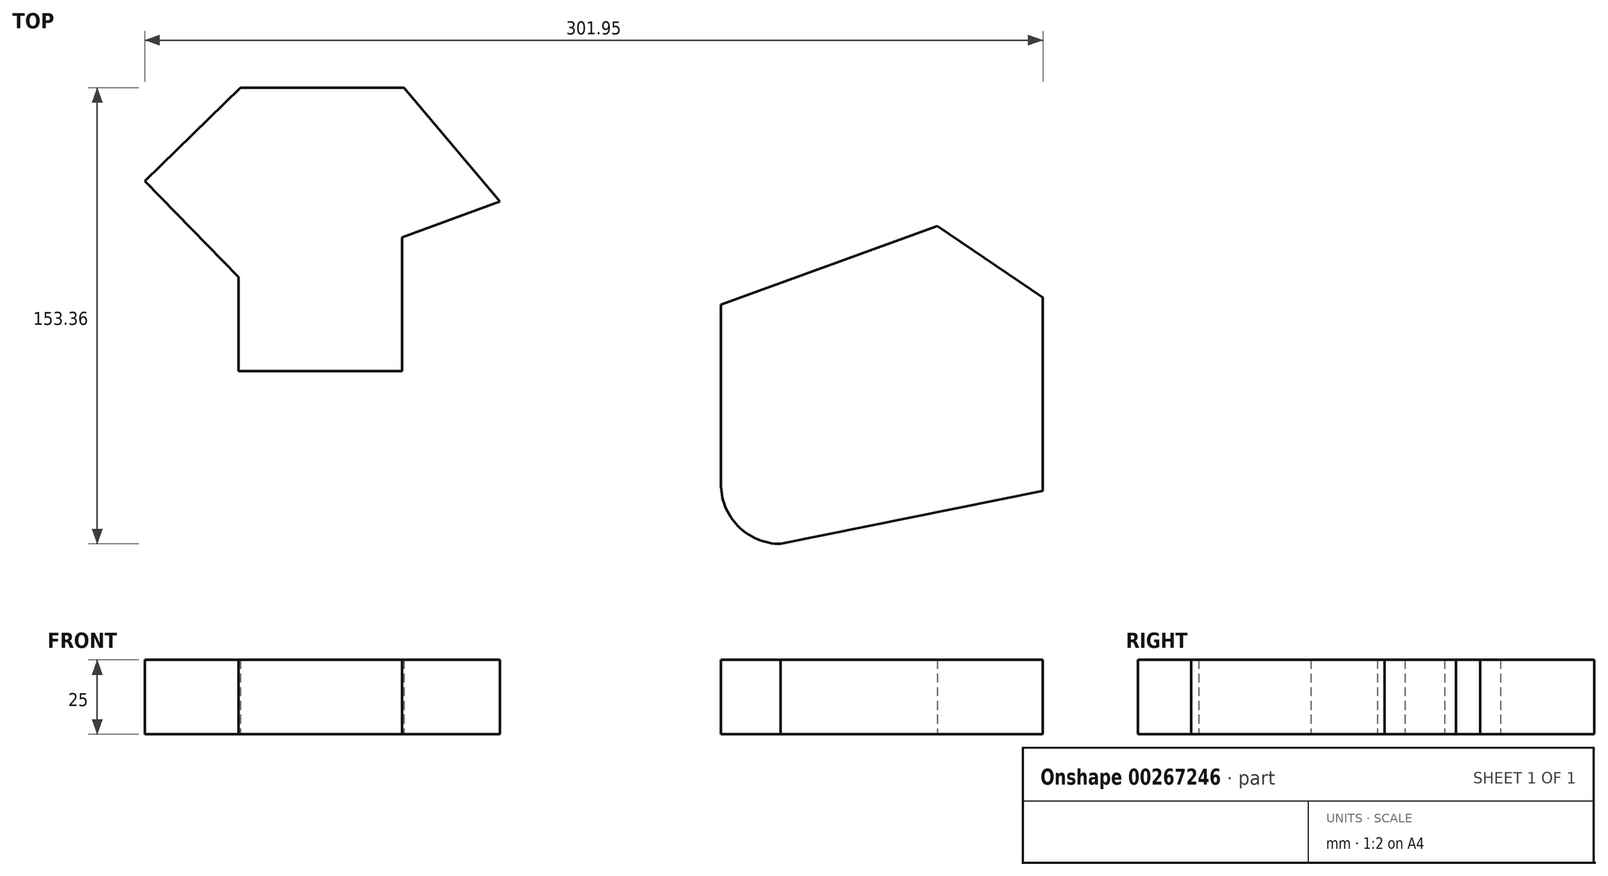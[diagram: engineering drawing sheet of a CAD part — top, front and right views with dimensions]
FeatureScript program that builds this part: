
annotation { "Feature Type Name" : "Feature", "Feature Type Description" : "" }
export const myFeature = defineFeature(function(context is Context, id is Id, definition is map)
    precondition{}
    {
        {
            var Q0;
            Q0=qCreatedBy(makeId("Top.planeOp"),FACE);
            var sketch = newSketch(context, id + "F0", { "sketchPlane" : qUnion([Q0])});
            skLineSegment(sketch, "E0", {"start": v(-58.1, 40.28) * mm, "end": v(-3.1, 40.28) * mm});
            skLineSegment(sketch, "E1", {"start": v(-3.1, 40.28) * mm, "end": v(-3.1, 85.28) * mm});
            skLineSegment(sketch, "E2", {"start": v(-3.1, 85.28) * mm, "end": v(29.78, 97.25) * mm});
            skLineSegment(sketch, "E3", {"start": v(29.78, 97.25) * mm, "end": v(-2.36, 135.55) * mm});
            skLineSegment(sketch, "E4", {"start": v(-2.36, 135.55) * mm, "end": v(-57.36, 135.55) * mm});
            skPoint(sketch, "E5.start.orphan", {"position": v(31.76, 97.25) * mm});
            skLineSegment(sketch, "E6", {"start": v(-57.36, 135.55) * mm, "end": v(-89.55, 104.1) * mm});
            skLineSegment(sketch, "E7", {"start": v(-89.55, 104.1) * mm, "end": v(-58.1, 71.92) * mm});
            skLineSegment(sketch, "E8", {"start": v(-58.1, 71.92) * mm, "end": v(-58.1, 40.28) * mm});
            skLineSegment(sketch, "E9", {"start": v(212.4, 0) * mm, "end": v(212.4, 65) * mm});
            skLineSegment(sketch, "E10", {"start": v(212.4, 65) * mm, "end": v(176.87, 89.05) * mm});
            skLineSegment(sketch, "E11", {"start": v(176.87, 89.05) * mm, "end": v(104.18, 62.6) * mm});
            skLineSegment(sketch, "E12", {"start": v(104.18, 62.6) * mm, "end": v(104.18, 2.6) * mm});
            skArc(sketch, "E13", {"start": v(104.18, 2.6) * mm, "mid": v(109.9, -11.81) * mm, "end": v(124.18, -17.81) * mm});
            skLineSegment(sketch, "E14", {"start": v(124.18, -17.81) * mm, "end": v(212.4, 0) * mm});
            skSolve(sketch);
        }
        {
            var Q0;
            Q0 = qSketchRegion(id + "F0", true);
            extrude(context, id + "F1", {"entities" : qUnion([Q0]), "depth" : 25 * mm});
        }
    });
